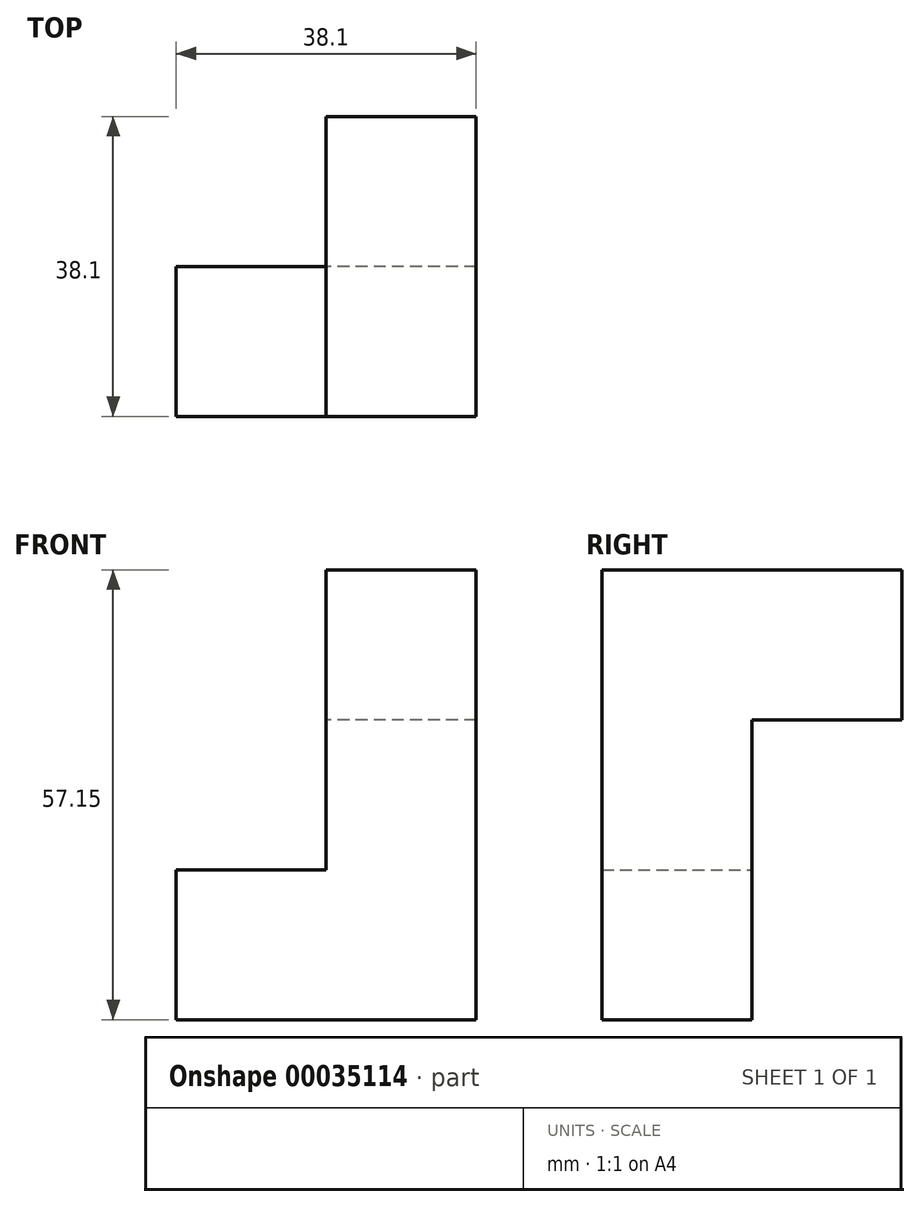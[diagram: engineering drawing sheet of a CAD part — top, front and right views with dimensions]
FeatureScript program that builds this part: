
annotation { "Feature Type Name" : "Feature", "Feature Type Description" : "" }
export const myFeature = defineFeature(function(context is Context, id is Id, definition is map)
    precondition{}
    {
        {
            var Q0;
            Q0=qCreatedBy(makeId("Top.planeOp"),FACE);
            var sketch = newSketch(context, id + "F0", { "sketchPlane" : qUnion([Q0])});
            skLineSegment(sketch, "E0.bottom", {"start": v(0, 0) * mm, "end": v(38.1, 0) * mm});
            skLineSegment(sketch, "E0.top", {"start": v(0, 19.05) * mm, "end": v(38.1, 19.05) * mm});
            skLineSegment(sketch, "E0.left", {"start": v(0, 0) * mm, "end": v(0, 19.05) * mm});
            skLineSegment(sketch, "E0.right", {"start": v(38.1, 0) * mm, "end": v(38.1, 19.05) * mm});
            skSolve(sketch);
        }
        {
            var Q0;
            Q0 = qSketchRegion(id + "F0", true);
            extrude(context, id + "F1", {"entities" : qUnion([Q0]), "depth" : 19.05 * mm});
        }
        {
            var Q0;
            Q0=makeQuery(id+"F1.opExtrude","CAP_FACE",FACE,{"disambiguationData":[OSD([sQuery(id+"F0.wireOp",EDGE,"E0.bottom"),sQuery(id+"F0.wireOp",EDGE,"E0.top"),sQuery(id+"F0.wireOp",EDGE,"E0.left"),sQuery(id+"F0.wireOp",EDGE,"E0.right")])],"isStart":false});
            var sketch = newSketch(context, id + "F2", { "sketchPlane" : qUnion([Q0])});
            skLineSegment(sketch, "E1.bottom", {"start": v(38.1, 19.05) * mm, "end": v(19.05, 19.05) * mm});
            skLineSegment(sketch, "E1.top", {"start": v(38.1, 0) * mm, "end": v(19.05, 0) * mm});
            skLineSegment(sketch, "E1.left", {"start": v(38.1, 19.05) * mm, "end": v(38.1, 0) * mm});
            skLineSegment(sketch, "E1.right", {"start": v(19.05, 19.05) * mm, "end": v(19.05, 0) * mm});
            skSolve(sketch);
        }
        {
            var Q0;
            Q0 = qSketchRegion(id + "F2", true);
            extrude(context, id + "F3", {"entities" : qUnion([Q0]), "operationType" : NewBodyOperationType.ADD, "depth" : 38.1 * mm});
        }
        {
            var Q0;
            Q0=makeQuery(id+"F3.boolean.opBoolean","MERGE",FACE,{"derivedFrom":[makeQuery(id+"F1.opExtrude","SWEPT_FACE",FACE,{"disambiguationData":[OSD([sQuery(id+"F0.wireOp",EDGE,"E0.top")])]}),makeQuery(id+"F3.opExtrude","SWEPT_FACE",FACE,{"disambiguationData":[OSD([sQuery(id+"F2.wireOp",EDGE,"E1.bottom")])]})]});
            var sketch = newSketch(context, id + "F4", { "sketchPlane" : qUnion([Q0])});
            skLineSegment(sketch, "E2.bottom", {"start": v(-38.1, 57.15) * mm, "end": v(-19.05, 57.15) * mm});
            skLineSegment(sketch, "E2.top", {"start": v(-38.1, 38.1) * mm, "end": v(-19.05, 38.1) * mm});
            skLineSegment(sketch, "E2.left", {"start": v(-38.1, 57.15) * mm, "end": v(-38.1, 38.1) * mm});
            skLineSegment(sketch, "E2.right", {"start": v(-19.05, 57.15) * mm, "end": v(-19.05, 38.1) * mm});
            skSolve(sketch);
        }
        {
            var Q0;
            Q0=makeQuery(id+"F4.imprint","IMPRINT",FACE,{"disambiguationData":[TD([[makeQuery(id+"F4.imprint","IMPRINT",EDGE,{"derivedFrom":sQuery(id+"F4.wireOp",EDGE,"E2.bottom")}),1.0]])]});
            extrude(context, id + "F5", {"entities" : qUnion([Q0]), "operationType" : NewBodyOperationType.ADD, "depth" : 19.05 * mm});
        }
    });
